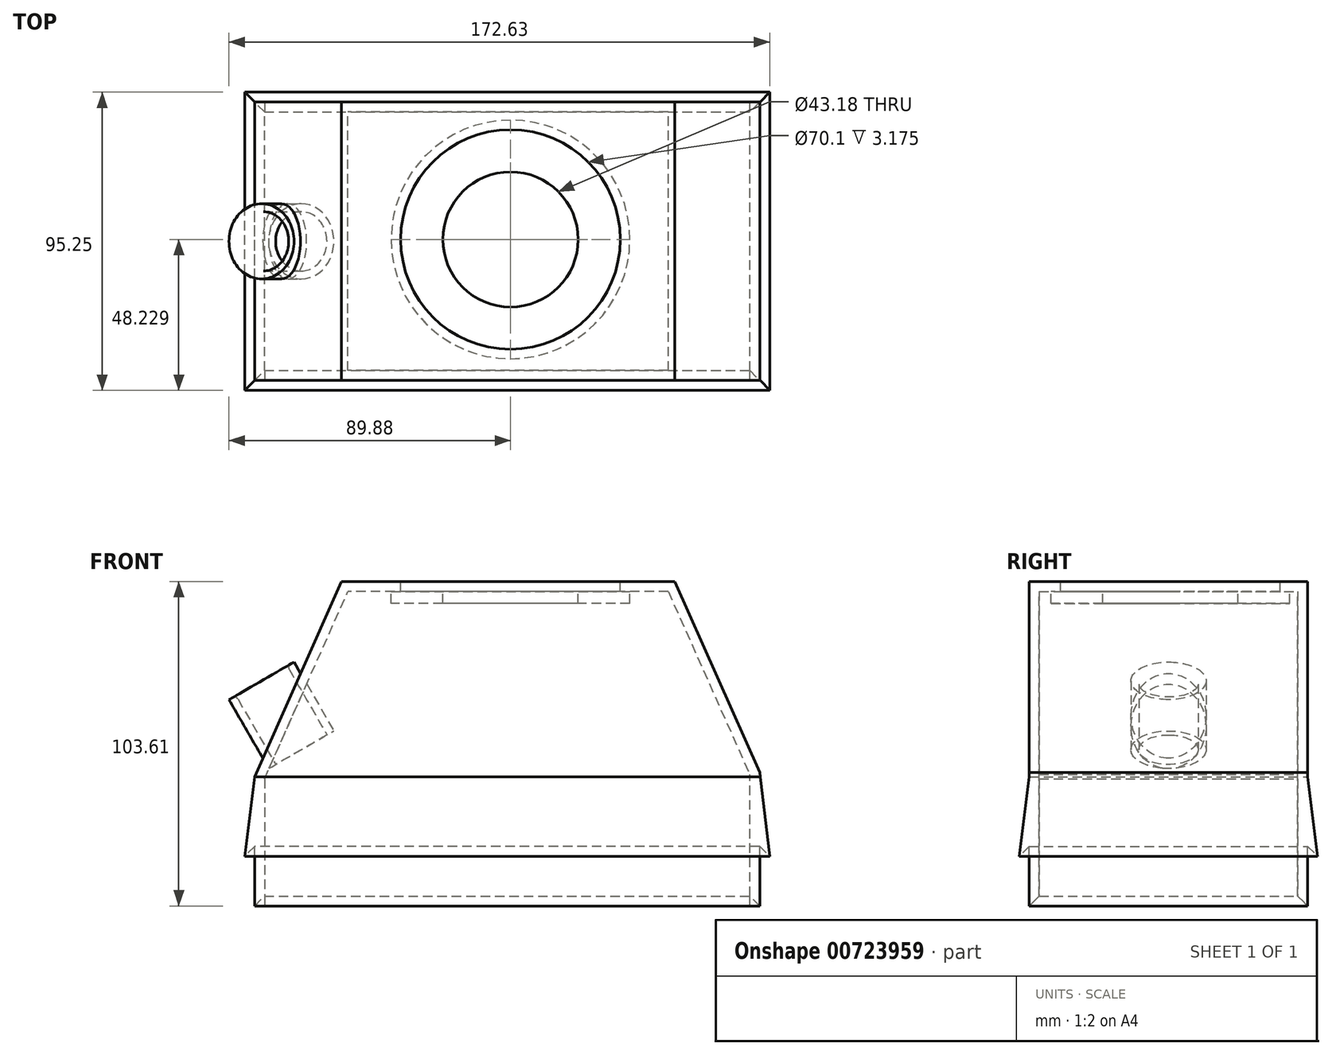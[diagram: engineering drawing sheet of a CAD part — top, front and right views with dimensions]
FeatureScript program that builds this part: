
annotation { "Feature Type Name" : "Feature", "Feature Type Description" : "" }
export const myFeature = defineFeature(function(context is Context, id is Id, definition is map)
    precondition{}
    {
        {
            var Q0;
            Q0=qCreatedBy(makeId("Front.planeOp"),FACE);
            var sketch = newSketch(context, id + "F0", { "sketchPlane" : qUnion([Q0])});
            skLineSegment(sketch, "E0", {"start": v(52.44, 212.53) * mm, "end": v(19.57, 212.53) * mm});
            skLineSegment(sketch, "E1", {"start": v(19.57, 212.53) * mm, "end": v(-53.96, 212.53) * mm});
            skPoint(sketch, "E2.visualSharp", {"position": v(52.59, 212.53) * mm});
            skLineSegment(sketch, "E3", {"start": v(-81.72, 124.8) * mm, "end": v(-81.72, 150.2) * mm});
            skLineSegment(sketch, "E4", {"start": v(-81.72, 150.2) * mm, "end": v(-53.96, 212.53) * mm});
            skLineSegment(sketch, "E5", {"start": v(79.57, 124.8) * mm, "end": v(79.57, 151.59) * mm});
            skLineSegment(sketch, "E6", {"start": v(52.44, 212.53) * mm, "end": v(79.57, 151.59) * mm});
            skLineSegment(sketch, "E7.0", {"start": v(76.4, 124.8) * mm, "end": v(76.4, 150.91) * mm});
            skLineSegment(sketch, "E7.1", {"start": v(50.38, 209.36) * mm, "end": v(76.4, 150.91) * mm});
            skLineSegment(sketch, "E7.2", {"start": v(-78.54, 124.8) * mm, "end": v(-78.54, 149.52) * mm});
            skLineSegment(sketch, "E7.3", {"start": v(-78.54, 149.52) * mm, "end": v(-51.9, 209.36) * mm});
            skLineSegment(sketch, "E7.4", {"start": v(19.62, 209.36) * mm, "end": v(-51.9, 209.36) * mm});
            skLineSegment(sketch, "E7.5", {"start": v(50.38, 209.36) * mm, "end": v(19.62, 209.36) * mm});
            skLineSegment(sketch, "E8", {"start": v(-81.72, 124.8) * mm, "end": v(-81.72, 112.1) * mm});
            skLineSegment(sketch, "E9", {"start": v(-78.54, 124.8) * mm, "end": v(-78.54, 112.1) * mm});
            skLineSegment(sketch, "E10", {"start": v(-78.54, 112.1) * mm, "end": v(-81.72, 108.92) * mm});
            skLineSegment(sketch, "E11", {"start": v(-81.72, 108.92) * mm, "end": v(-81.72, 112.1) * mm});
            skLineSegment(sketch, "E12", {"start": v(79.57, 124.8) * mm, "end": v(79.57, 112.1) * mm});
            skLineSegment(sketch, "E13", {"start": v(76.4, 124.8) * mm, "end": v(76.4, 112.1) * mm});
            skLineSegment(sketch, "E14", {"start": v(76.4, 112.1) * mm, "end": v(79.57, 108.92) * mm});
            skPoint(sketch, "E14.endSnap0", {"position": v(79.57, 118.44) * mm});
            skLineSegment(sketch, "E15", {"start": v(79.57, 108.92) * mm, "end": v(79.57, 112.1) * mm});
            skLineSegment(sketch, "E16", {"start": v(-81.72, 150.2) * mm, "end": v(-84.9, 124.8) * mm});
            skLineSegment(sketch, "E17", {"start": v(-84.9, 124.8) * mm, "end": v(-81.72, 127.97) * mm});
            skLineSegment(sketch, "E18", {"start": v(79.57, 151.59) * mm, "end": v(82.75, 124.8) * mm});
            skLineSegment(sketch, "E19", {"start": v(82.75, 124.8) * mm, "end": v(79.57, 127.97) * mm});
            skPoint(sketch, "E20.endSnap0", {"position": v(81.16, 126.38) * mm});
            skLineSegment(sketch, "E21", {"start": v(79.57, 124.8) * mm, "end": v(82.75, 124.8) * mm, "construction": true});
            skLineSegment(sketch, "E22", {"start": v(-81.72, 108.92) * mm, "end": v(79.57, 108.92) * mm});
            skSolve(sketch);
        }
        {
            var Q0;
            Q0=makeQuery(id+"F0.imprint","IMPRINT",FACE,{"disambiguationData":[TD([[makeQuery(id+"F0.imprint","IMPRINT",EDGE,{"derivedFrom":sQuery(id+"F0.wireOp",EDGE,"E0")}),1.0]])]});
            extrude(context, id + "F1", {"entities" : qUnion([Q0]), "depth" : 82.55 * mm, "offsetDistance" : 25.4 * mm});
        }
        {
            var Q0;
            Q0=makeQuery(id+"F0.imprint","IMPRINT",FACE,{"disambiguationData":[TD([[makeQuery(id+"F0.imprint","IMPRINT",EDGE,{"derivedFrom":sQuery(id+"F0.wireOp",EDGE,"E0")}),1.0]])]});
            var Q1;
            Q1=makeQuery(id+"F0.imprint","IMPRINT",FACE,{"disambiguationData":[TD([[makeQuery(id+"F0.imprint","IMPRINT",EDGE,{"derivedFrom":sQuery(id+"F0.wireOp",EDGE,"E7.0")}),1.0]])]});
            extrude(context, id + "F2", {"entities" : qUnion([Q0, Q1]), "operationType" : NewBodyOperationType.ADD, "oppositeDirection" : true, "depth" : 3.17 * mm, "offsetDistance" : 25.4 * mm});
        }
        {
            var Q0;
            Q0=makeQuery(id+"F0.imprint","IMPRINT",FACE,{"disambiguationData":[TD([[makeQuery(id+"F0.imprint","IMPRINT",EDGE,{"derivedFrom":sQuery(id+"F0.wireOp",EDGE,"E7.0")}),1.0]])]});
            var Q1;
            Q1=makeQuery(id+"F0.imprint","IMPRINT",FACE,{"disambiguationData":[TD([[makeQuery(id+"F0.imprint","IMPRINT",EDGE,{"derivedFrom":sQuery(id+"F0.wireOp",EDGE,"E0")}),1.0]])]});
            extrude(context, id + "F3", {"entities" : qUnion([Q0, Q1]), "operationType" : NewBodyOperationType.ADD, "depth" : 85.72 * mm, "offsetDistance" : 25.4 * mm, "hasSecondDirection" : true, "secondDirectionOppositeDirection" : false, "secondDirectionDepth" : 82.55 * mm});
        }
        {
            var Q0;
            Q0=qCreatedBy(makeId("Right.planeOp"),FACE);
            var sketch = newSketch(context, id + "F4", { "sketchPlane" : qUnion([Q0])});
            skPoint(sketch, "E23.0", {"position": v(-82.55, 112.1) * mm});
            skPoint(sketch, "E24.0", {"position": v(-82.55, 108.92) * mm});
            skPoint(sketch, "E25.0", {"position": v(-85.73, 108.92) * mm});
            skLineSegment(sketch, "E26", {"start": v(-85.72, 108.92) * mm, "end": v(-82.55, 112.1) * mm});
            skLineSegment(sketch, "E27", {"start": v(-82.55, 112.1) * mm, "end": v(-82.55, 108.92) * mm});
            skLineSegment(sketch, "E28", {"start": v(-82.55, 108.92) * mm, "end": v(-85.72, 108.92) * mm});
            skPoint(sketch, "E29.0", {"position": v(0, 112.1) * mm});
            skPoint(sketch, "E30.0", {"position": v(0, 108.92) * mm});
            skPoint(sketch, "E31.0", {"position": v(3.18, 108.92) * mm});
            skLineSegment(sketch, "E32", {"start": v(0, 112.1) * mm, "end": v(3.17, 108.92) * mm});
            skLineSegment(sketch, "E33", {"start": v(3.17, 108.92) * mm, "end": v(0, 108.92) * mm});
            skLineSegment(sketch, "E34", {"start": v(0, 108.92) * mm, "end": v(0, 112.1) * mm});
            skSolve(sketch);
        }
        {
            var Q0;
            Q0 = qSketchRegion(id + "F4", true);
            var Q1;
            Q1=makeQuery(id+"F1.opExtrude","SWEPT_FACE",FACE,{"disambiguationData":[OSD([sQuery(id+"F0.wireOp",EDGE,"E7.2"),sQuery(id+"F0.wireOp",EDGE,"E9")])]});
            var Q2;
            Q2=makeQuery(id+"F1.opExtrude","SWEPT_FACE",FACE,{"disambiguationData":[OSD([sQuery(id+"F0.wireOp",EDGE,"E7.0"),sQuery(id+"F0.wireOp",EDGE,"E13")])]});
            extrude(context, id + "F5", {"entities" : qUnion([Q0]), "operationType" : NewBodyOperationType.REMOVE, "endBound" : BoundingType.UP_TO_SURFACE, "oppositeDirection" : true, "depth" : 77.72 * mm, "endBoundEntityFace" : qUnion([Q1]), "offsetDistance" : 25.4 * mm, "hasSecondDirection" : true, "secondDirectionBound" : BoundingType.UP_TO_SURFACE, "secondDirectionOppositeDirection" : false, "secondDirectionDepth" : 25.4 * mm, "secondDirectionBoundEntityFace" : qUnion([Q2])});
        }
        {
            var Q0;
            Q0=makeQuery(id+"F5.boolean.opBoolean","COPY",EDGE,{"derivedFrom":makeQuery(id+"F5.opExtrude","CAP_EDGE",EDGE,{"disambiguationData":[OSD([sQuery(id+"F4.wireOp",EDGE,"E33")])],"isStart":true})});
            var Q1;
            {var subQ3=sQuery(id+"F0.wireOp",EDGE,"E22");Q1=makeQuery(id+"F5.boolean.opBoolean","SPLIT",EDGE,{"disambiguationData":[TD([makeQuery(id+"F1.opExtrude","SWEPT_FACE",FACE,{"disambiguationData":[OSD([sQuery(id+"F0.wireOp",EDGE,"E14")])]})])],"derivedFrom":makeQuery(id+"F2.opExtrude","CAP_EDGE",EDGE,{"disambiguationData":[OSD([subQ3])],"isStart":true})});}
            var Q2;
            Q2=makeQuery(id+"F5.boolean.opBoolean","COPY",EDGE,{"derivedFrom":makeQuery(id+"F5.opExtrude","CAP_EDGE",EDGE,{"disambiguationData":[OSD([sQuery(id+"F4.wireOp",EDGE,"E28")])],"isStart":true})});
            var Q3;
            {var subQ0=sQuery(id+"F0.wireOp",EDGE,"E22");Q3=makeQuery(id+"F5.boolean.opBoolean","SPLIT",EDGE,{"disambiguationData":[TD([makeQuery(id+"F1.opExtrude","SWEPT_FACE",FACE,{"disambiguationData":[OSD([sQuery(id+"F0.wireOp",EDGE,"E14")])]})])],"derivedFrom":makeQuery(id+"F3.opExtrude","CAP_EDGE",EDGE,{"disambiguationData":[OSD([subQ0])],"isStart":true})});}
            var Q4;
            Q4=makeQuery(id+"F5.boolean.opBoolean","COPY",EDGE,{"derivedFrom":makeQuery(id+"F5.opExtrude","CAP_EDGE",EDGE,{"disambiguationData":[OSD([sQuery(id+"F4.wireOp",EDGE,"E33")])],"isStart":false})});
            var Q5;
            {var subQ3=sQuery(id+"F0.wireOp",EDGE,"E22");Q5=makeQuery(id+"F5.boolean.opBoolean","SPLIT",EDGE,{"disambiguationData":[TD([makeQuery(id+"F1.opExtrude","SWEPT_FACE",FACE,{"disambiguationData":[OSD([sQuery(id+"F0.wireOp",EDGE,"E10")])]})])],"derivedFrom":makeQuery(id+"F2.opExtrude","CAP_EDGE",EDGE,{"disambiguationData":[OSD([subQ3])],"isStart":true})});}
            var Q6;
            Q6=makeQuery(id+"F5.boolean.opBoolean","COPY",EDGE,{"derivedFrom":makeQuery(id+"F5.opExtrude","CAP_EDGE",EDGE,{"disambiguationData":[OSD([sQuery(id+"F4.wireOp",EDGE,"E28")])],"isStart":false})});
            var Q7;
            {var subQ0=sQuery(id+"F0.wireOp",EDGE,"E22");Q7=makeQuery(id+"F5.boolean.opBoolean","SPLIT",EDGE,{"disambiguationData":[TD([makeQuery(id+"F1.opExtrude","SWEPT_FACE",FACE,{"disambiguationData":[OSD([sQuery(id+"F0.wireOp",EDGE,"E10")])]})])],"derivedFrom":makeQuery(id+"F3.opExtrude","CAP_EDGE",EDGE,{"disambiguationData":[OSD([subQ0])],"isStart":true})});}
            chamfer(context, id + "F6", {"entities" : qUnion([Q0, Q1, Q2, Q3, Q4, Q5, Q6, Q7]), "chamferType" : ChamferType.OFFSET_ANGLE, "width" : 3.17 * mm, "oppositeDirection" : false, "angle" : 45 * degree});
        }
        {
            var Q0;
            {var subQ0=sQuery(id+"F0.wireOp",EDGE,"E18");Q0=makeQuery(id+"F0.imprint","IMPRINT",FACE,{"disambiguationData":[TD([[makeQuery(id+"F0.imprint","IMPRINT",EDGE,{"derivedFrom":subQ0}),-1.0]])]});}
            var Q1;
            {var subQ0=sQuery(id+"F0.wireOp",EDGE,"E16");Q1=makeQuery(id+"F0.imprint","IMPRINT",FACE,{"disambiguationData":[TD([[makeQuery(id+"F0.imprint","IMPRINT",EDGE,{"derivedFrom":subQ0}),1.0]])]});}
            var Q2;
            Q2=makeQuery(id+"F3.opExtrude","CAP_FACE",FACE,{"disambiguationData":[OSD([sQuery(id+"F0.wireOp",EDGE,"E0"),sQuery(id+"F0.wireOp",EDGE,"E1"),sQuery(id+"F0.wireOp",EDGE,"E3"),sQuery(id+"F0.wireOp",EDGE,"E4"),sQuery(id+"F0.wireOp",EDGE,"E5"),sQuery(id+"F0.wireOp",EDGE,"E6"),sQuery(id+"F0.wireOp",EDGE,"E8"),sQuery(id+"F0.wireOp",EDGE,"E11"),sQuery(id+"F0.wireOp",EDGE,"E12"),sQuery(id+"F0.wireOp",EDGE,"E15"),sQuery(id+"F0.wireOp",EDGE,"E22")])],"isStart":false});
            var Q3;
            Q3=makeQuery(id+"F2.opExtrude","CAP_FACE",FACE,{"disambiguationData":[OSD([sQuery(id+"F0.wireOp",EDGE,"E0"),sQuery(id+"F0.wireOp",EDGE,"E1"),sQuery(id+"F0.wireOp",EDGE,"E3"),sQuery(id+"F0.wireOp",EDGE,"E4"),sQuery(id+"F0.wireOp",EDGE,"E5"),sQuery(id+"F0.wireOp",EDGE,"E6"),sQuery(id+"F0.wireOp",EDGE,"E8"),sQuery(id+"F0.wireOp",EDGE,"E11"),sQuery(id+"F0.wireOp",EDGE,"E12"),sQuery(id+"F0.wireOp",EDGE,"E15"),sQuery(id+"F0.wireOp",EDGE,"E22")])],"isStart":false});
            extrude(context, id + "F7", {"entities" : qUnion([Q0, Q1]), "operationType" : NewBodyOperationType.ADD, "endBound" : BoundingType.UP_TO_SURFACE, "depth" : 25.4 * mm, "endBoundEntityFace" : qUnion([Q2]), "offsetDistance" : 25.4 * mm, "hasSecondDirection" : true, "secondDirectionBound" : BoundingType.UP_TO_SURFACE, "secondDirectionOppositeDirection" : true, "secondDirectionDepth" : 25.4 * mm, "secondDirectionBoundEntityFace" : qUnion([Q3])});
        }
        {
            var Q0;
            Q0=qCreatedBy(makeId("Right.planeOp"),FACE);
            var sketch = newSketch(context, id + "F8", { "sketchPlane" : qUnion([Q0])});
            skPoint(sketch, "E35.0", {"position": v(3.17, 127.97) * mm});
            skPoint(sketch, "E36.0", {"position": v(3.17, 124.8) * mm});
            skLineSegment(sketch, "E37", {"start": v(3.17, 124.8) * mm, "end": v(6.35, 124.8) * mm, "construction": true});
            skLineSegment(sketch, "E38", {"start": v(6.35, 124.8) * mm, "end": v(3.17, 127.97) * mm});
            skPoint(sketch, "E39.0", {"position": v(-85.73, 124.8) * mm});
            skPoint(sketch, "E40.0", {"position": v(-85.73, 127.97) * mm});
            skLineSegment(sketch, "E41", {"start": v(-85.73, 124.8) * mm, "end": v(-88.9, 124.8) * mm, "construction": true});
            skLineSegment(sketch, "E42", {"start": v(-88.9, 124.8) * mm, "end": v(-85.73, 127.97) * mm});
            skLineSegment(sketch, "E43", {"start": v(-85.73, 127.97) * mm, "end": v(-85.73, 150.2) * mm});
            skPoint(sketch, "E44.0", {"position": v(-85.73, 150.2) * mm});
            skLineSegment(sketch, "E45", {"start": v(-85.73, 150.2) * mm, "end": v(-88.9, 124.8) * mm});
            skPoint(sketch, "E46.0", {"position": v(3.18, 150.2) * mm});
            skLineSegment(sketch, "E47", {"start": v(3.18, 150.2) * mm, "end": v(3.17, 127.97) * mm});
            skLineSegment(sketch, "E48", {"start": v(3.17, 150.2) * mm, "end": v(6.35, 124.8) * mm});
            skSolve(sketch);
        }
        {
            var Q0;
            Q0=makeQuery(id+"F8.imprint","IMPRINT",FACE,{"disambiguationData":[TD([[makeQuery(id+"F8.imprint","IMPRINT",EDGE,{"derivedFrom":sQuery(id+"F8.wireOp",EDGE,"E42")}),1.0]])]});
            var Q1;
            Q1=makeQuery(id+"F8.imprint","IMPRINT",FACE,{"disambiguationData":[TD([[makeQuery(id+"F8.imprint","IMPRINT",EDGE,{"derivedFrom":sQuery(id+"F8.wireOp",EDGE,"E38")}),-1.0]])]});
            var Q2;
            Q2=makeQuery(id+"F7.opExtrude","SWEPT_FACE",FACE,{"disambiguationData":[OSD([sQuery(id+"F0.wireOp",EDGE,"E18")])]});
            var Q3;
            Q3=makeQuery(id+"F7.opExtrude","SWEPT_FACE",FACE,{"disambiguationData":[OSD([sQuery(id+"F0.wireOp",EDGE,"E16")])]});
            extrude(context, id + "F9", {"entities" : qUnion([Q0, Q1]), "operationType" : NewBodyOperationType.ADD, "endBound" : BoundingType.UP_TO_SURFACE, "depth" : 25.4 * mm, "endBoundEntityFace" : qUnion([Q2]), "offsetDistance" : 25.4 * mm, "hasSecondDirection" : true, "secondDirectionBound" : BoundingType.UP_TO_SURFACE, "secondDirectionOppositeDirection" : true, "secondDirectionDepth" : 25.4 * mm, "secondDirectionBoundEntityFace" : qUnion([Q3])});
        }
        {
            var Q0;
            Q0=qCreatedBy(makeId("Front.planeOp"),FACE);
            var sketch = newSketch(context, id + "F10", { "sketchPlane" : qUnion([Q0])});
            skPoint(sketch, "E49.0", {"position": v(82.75, 124.8) * mm});
            skPoint(sketch, "E50.0", {"position": v(79.57, 127.97) * mm});
            skPoint(sketch, "E51.0", {"position": v(82.37, 127.97) * mm});
            skPoint(sketch, "E52.0", {"position": v(-84.5, 127.97) * mm});
            skPoint(sketch, "E53.0", {"position": v(-84.9, 124.8) * mm});
            skPoint(sketch, "E54.0", {"position": v(-81.72, 127.97) * mm});
            skLineSegment(sketch, "E55.0", {"start": v(-84.9, 124.8) * mm, "end": v(-81.72, 127.97) * mm});
            skLineSegment(sketch, "E56.0", {"start": v(-84.5, 127.97) * mm, "end": v(-84.9, 124.8) * mm});
            skLineSegment(sketch, "E57.0", {"start": v(-81.72, 127.97) * mm, "end": v(-84.5, 127.97) * mm});
            skLineSegment(sketch, "E58.0", {"start": v(82.75, 124.8) * mm, "end": v(79.57, 127.97) * mm});
            skPoint(sketch, "E59.0", {"position": v(80.97, 127.97) * mm});
            skLineSegment(sketch, "E60.0", {"start": v(82.37, 127.97) * mm, "end": v(79.57, 127.97) * mm});
            skLineSegment(sketch, "E61.0", {"start": v(82.37, 127.97) * mm, "end": v(82.75, 124.8) * mm});
            skSolve(sketch);
        }
        {
            var Q0;
            Q0 = qSketchRegion(id + "F10", true);
            var Q1;
            Q1=makeQuery(id+"F9.opExtrude","SWEPT_FACE",FACE,{"disambiguationData":[OSD([sQuery(id+"F8.wireOp",EDGE,"E38")])]});
            var Q2;
            Q2=makeQuery(id+"F9.opExtrude","SWEPT_FACE",FACE,{"disambiguationData":[OSD([sQuery(id+"F8.wireOp",EDGE,"E42")])]});
            extrude(context, id + "F11", {"entities" : qUnion([Q0]), "operationType" : NewBodyOperationType.ADD, "endBound" : BoundingType.UP_TO_SURFACE, "oppositeDirection" : true, "depth" : 25.4 * mm, "endBoundEntityFace" : qUnion([Q1]), "offsetDistance" : 25.4 * mm, "hasSecondDirection" : true, "secondDirectionBound" : BoundingType.UP_TO_SURFACE, "secondDirectionOppositeDirection" : false, "secondDirectionDepth" : 25.4 * mm, "secondDirectionBoundEntityFace" : qUnion([Q2])});
        }
        {
            var Q0;
            {var subQ0=sQuery(id+"F0.wireOp",EDGE,"E1");var subQ1=sQuery(id+"F0.wireOp",EDGE,"E0");Q0=makeQuery(id+"F3.boolean.opBoolean","MERGE",FACE,{"derivedFrom":[makeQuery(id+"F2.boolean.opBoolean","MERGE",FACE,{"derivedFrom":[makeQuery(id+"F1.opExtrude","SWEPT_FACE",FACE,{"disambiguationData":[OSD([subQ1,subQ0])]}),makeQuery(id+"F2.opExtrude","SWEPT_FACE",FACE,{"disambiguationData":[OSD([subQ1,subQ0])]})]}),makeQuery(id+"F3.opExtrude","SWEPT_FACE",FACE,{"disambiguationData":[OSD([subQ1,subQ0])]})]});}
            var sketch = newSketch(context, id + "F12", { "sketchPlane" : qUnion([Q0])});
            skPoint(sketch, "E62", {"position": v(0, -40.67) * mm});
            skCircle(sketch, "E63", {"center": v(0, -40.67) * mm, "radius": 21.59 * mm});
            skSolve(sketch);
        }
        {
            var Q0;
            Q0=makeQuery(id+"F12.imprint","IMPRINT",FACE,{"disambiguationData":[TD([[makeQuery(id+"F12.imprint","IMPRINT",EDGE,{"derivedFrom":sQuery(id+"F12.wireOp",EDGE,"E63")}),1.0]])]});
            extrude(context, id + "F13", {"entities" : qUnion([Q0]), "operationType" : NewBodyOperationType.REMOVE, "oppositeDirection" : true, "depth" : 5.08 * mm, "offsetDistance" : 25.4 * mm});
        }
        {
            var Q0;
            {var subQ0=sQuery(id+"F0.wireOp",EDGE,"E1");var subQ1=sQuery(id+"F0.wireOp",EDGE,"E0");Q0=makeQuery(id+"F3.boolean.opBoolean","MERGE",FACE,{"derivedFrom":[makeQuery(id+"F2.boolean.opBoolean","MERGE",FACE,{"derivedFrom":[makeQuery(id+"F1.opExtrude","SWEPT_FACE",FACE,{"disambiguationData":[OSD([subQ1,subQ0])]}),makeQuery(id+"F2.opExtrude","SWEPT_FACE",FACE,{"disambiguationData":[OSD([subQ1,subQ0])]})]}),makeQuery(id+"F3.opExtrude","SWEPT_FACE",FACE,{"disambiguationData":[OSD([subQ1,subQ0])]})]});}
            var sketch = newSketch(context, id + "F14", { "sketchPlane" : qUnion([Q0])});
            skCircle(sketch, "E64", {"center": v(0, -40.67) * mm, "radius": 35.05 * mm});
            skCircle(sketch, "E65", {"center": v(0, -40.67) * mm, "radius": 38.1 * mm});
            skSolve(sketch);
        }
        {
            var Q0;
            Q0=makeQuery(id+"F14.imprint","IMPRINT",FACE,{"disambiguationData":[TD([[makeQuery(id+"F14.imprint","IMPRINT",EDGE,{"derivedFrom":sQuery(id+"F14.wireOp",EDGE,"E64")}),-1.0]])]});
            var Q1;
            Q1=makeQuery(id+"F14.imprint","IMPRINT",FACE,{"disambiguationData":[TD([[makeQuery(id+"F14.imprint","IMPRINT",EDGE,{"derivedFrom":sQuery(id+"F14.wireOp",EDGE,"E64")}),1.0]])]});
            extrude(context, id + "F15", {"entities" : qUnion([Q0, Q1]), "operationType" : NewBodyOperationType.ADD, "oppositeDirection" : true, "depth" : 7 * mm, "offsetDistance" : 25.4 * mm});
        }
        {
            var Q0;
            Q0=makeQuery(id+"F14.imprint","IMPRINT",FACE,{"disambiguationData":[TD([[makeQuery(id+"F14.imprint","IMPRINT",EDGE,{"derivedFrom":sQuery(id+"F14.wireOp",EDGE,"E64")}),1.0]])]});
            extrude(context, id + "F16", {"entities" : qUnion([Q0]), "operationType" : NewBodyOperationType.REMOVE, "oppositeDirection" : true, "depth" : 3.17 * mm, "offsetDistance" : 25.4 * mm});
        }
        {
            var Q0;
            Q0=qCreatedBy(makeId("Right.planeOp"),FACE);
            var Q1;
            {var subQ0=sQuery(id+"F0.wireOp",EDGE,"E16");var subQ1=sQuery(id+"F0.wireOp",EDGE,"E4");var subQ2=sQuery(id+"F0.wireOp",EDGE,"E3");Q1=makeQuery(id+"F7.boolean.opBoolean","MERGE",EDGE,{"derivedFrom":[makeQuery(id+"F3.boolean.opBoolean","MERGE",EDGE,{"derivedFrom":[makeQuery(id+"F2.boolean.opBoolean","MERGE",EDGE,{"derivedFrom":[makeQuery(id+"F1.opExtrude","SWEPT_EDGE",EDGE,{"disambiguationData":[OSD([subQ2,subQ1,subQ0])]}),makeQuery(id+"F2.opExtrude","SWEPT_EDGE",EDGE,{"disambiguationData":[OSD([subQ2,subQ1,subQ0])]})]}),makeQuery(id+"F3.opExtrude","SWEPT_EDGE",EDGE,{"disambiguationData":[OSD([subQ2,subQ1,subQ0])]})]}),makeQuery(id+"F7.opExtrude","TWEAK_EDGE",EDGE,{"derivedFrom":[makeQuery(id+"F0.imprint","IMPRINT",EDGE,{"disambiguationData":[TD([[makeQuery(id+"F0.imprint","INTERSECT",VERTEX,{"derivedFrom":[subQ2,sQuery(id+"F0.wireOp",EDGE,"E17")]}),-1.0]])],"derivedFrom":subQ2}),makeQuery(id+"F0.imprint","IMPRINT",EDGE,{"derivedFrom":subQ0})]})]});}
            cPlane(context, id + "F17", {"entities" : qUnion([Q0, Q1]), "cplaneType" : CPlaneType.LINE_ANGLE, "offset" : 25.4 * mm, "angle" : 60 * degree, "width" : 152.4 * mm, "height" : 152.4 * mm});
        }
        {
            var Q0;
            Q0=qCreatedBy(id+"F17.planeOp",FACE);
            var sketch = newSketch(context, id + "F18", { "sketchPlane" : qUnion([Q0])});
            skLineSegment(sketch, "E66.0", {"start": v(4.33, -85.73) * mm, "end": v(4.33, 3.17) * mm});
            skPoint(sketch, "E67", {"position": v(4.33, -41.28) * mm});
            skCircle(sketch, "E68", {"center": v(21.56, -41.28) * mm, "radius": 9.46 * mm});
            skCircle(sketch, "E69", {"center": v(21.56, -41.28) * mm, "radius": 12001.5 * mm});
            skCircle(sketch, "E70", {"center": v(21.56, -41.28) * mm, "radius": 12 * mm});
            skSolve(sketch);
        }
        {
            var Q0;
            Q0=makeQuery(id+"F18.imprint","IMPRINT",FACE,{"disambiguationData":[TD([[makeQuery(id+"F18.imprint","IMPRINT",EDGE,{"derivedFrom":sQuery(id+"F18.wireOp",EDGE,"E68")}),-1.0]])]});
            extrude(context, id + "F19", {"entities" : qUnion([Q0]), "operationType" : NewBodyOperationType.ADD, "depth" : 25.4 * mm, "offsetDistance" : 25.4 * mm});
        }
        {
            var Q0;
            Q0=makeQuery(id+"F18.imprint","IMPRINT",FACE,{"disambiguationData":[TD([[makeQuery(id+"F18.imprint","IMPRINT",EDGE,{"derivedFrom":sQuery(id+"F18.wireOp",EDGE,"E68")}),1.0]])]});
            extrude(context, id + "F20", {"entities" : qUnion([Q0]), "operationType" : NewBodyOperationType.REMOVE, "depth" : 25.4 * mm, "offsetDistance" : 25.4 * mm});
        }
        {
            var Q0;
            Q0=makeQuery(id+"F19.opExtrude","CAP_EDGE",EDGE,{"disambiguationData":[OSD([sQuery(id+"F18.wireOp",EDGE,"E68")])],"isStart":false});
            fillet(context, id + "F21", {"entities" : qUnion([Q0]), "radius" : 1.27 * mm, "tangentPropagation" : true, "allowEdgeOverflow" : false});
        }
    });
